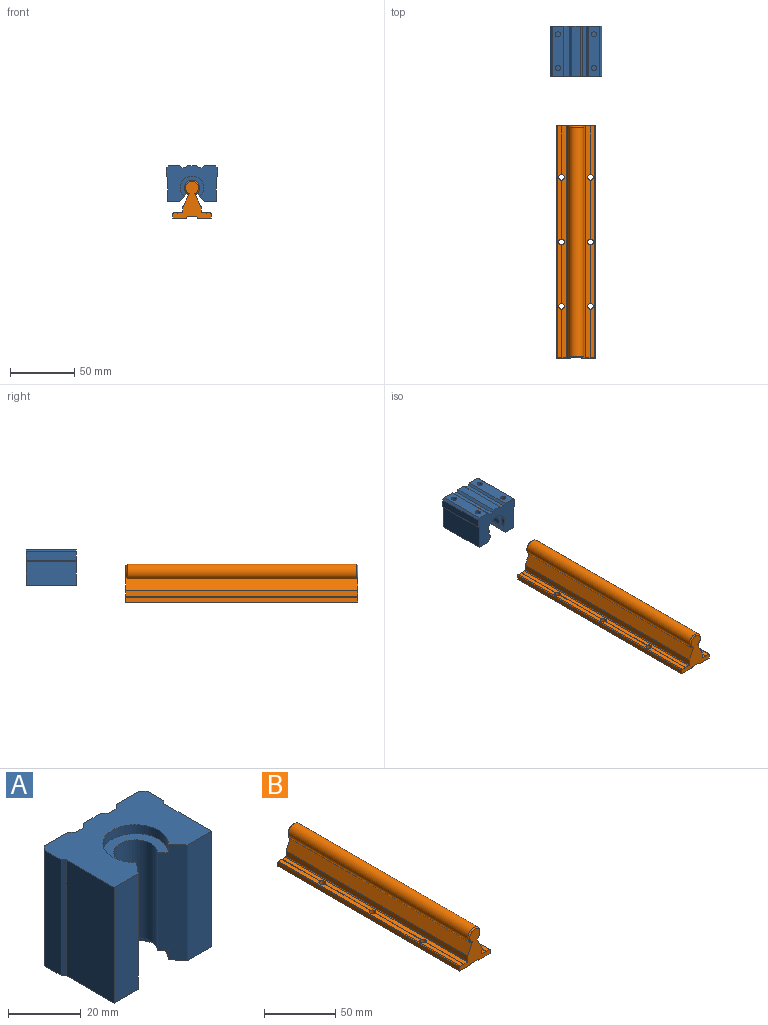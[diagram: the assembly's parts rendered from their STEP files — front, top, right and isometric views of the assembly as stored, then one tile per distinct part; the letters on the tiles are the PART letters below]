
ASSEMBLY  parts=2 mates=1
PART A: 36 faces, bbox 40x27.6x39 mm
  f0: cylinder r=6mm len=33mm, axis (0,0,-1), area 932.4mm2, adj f3,f4,f25,f35
  f1: plane 39x18.6mm, normal (-1,0,0), area 725.4mm2, adj f2,f21,f22,f23
  f2: plane 39x9.41mm, normal (0,-1,0), area 367mm2, adj f1,f3,f22,f23
  f3: plane 39x6.36mm, normal (0.77,-0.64,0), area 306mm2, adj f0,f2,f22,f23,f24,f25,f34,f35
  f4: plane 39x6.36mm, normal (-0.77,-0.64,0), area 306mm2, adj f0,f5,f22,f23,f24,f25,f34,f35
  f5: plane 39x9.41mm, normal (0,-1,0), area 367mm2, adj f4,f6,f22,f23
  f6: plane 39x18.6mm, normal (1,0,0), area 725.4mm2, adj f5,f7,f22,f23
  f7: plane 39x1mm, normal (0.71,-0.71,0), area 55.2mm2, adj f6,f8,f22,f23
  f8: plane 39x6.5mm, normal (1,0,0), area 253.5mm2, adj f7,f9,f22,f23
  f9: plane 39x1.5mm, normal (0.71,0.71,0), area 82.7mm2, adj f8,f10,f22,f23
  f10: plane 39x9mm, normal (0,1,0), area 325.9mm2, adj f9,f11,f22,f23,f30,f32
  f11: plane 39x1.62mm, normal (-0.68,0.73,0), area 86mm2, adj f10,f12,f22,f23
  f12: plane 39x3mm, normal (0,1,0), area 117mm2, adj f11,f13,f22,f23
  f13: plane 39x1.62mm, normal (0.68,0.73,0), area 86mm2, adj f12,f14,f22,f23
  f14: plane 39x6.53mm, normal (0,1,0), area 254.8mm2, adj f13,f15,f22,f23
  f15: plane 39x1.62mm, normal (-0.68,0.73,0), area 86mm2, adj f14,f16,f22,f23
  f16: plane 39x3mm, normal (0,1,0), area 117mm2, adj f15,f17,f22,f23
  f17: plane 39x1.62mm, normal (0.68,0.73,0), area 86mm2, adj f16,f18,f22,f23
  f18: plane 39x9mm, normal (0,1,0), area 325.9mm2, adj f17,f19,f22,f23,f26,f28
  f19: plane 39x1.5mm, normal (-0.71,0.71,0), area 82.7mm2, adj f18,f20,f22,f23
  f20: plane 39x6.5mm, normal (-1,0,0), area 253.5mm2, adj f19,f21,f22,f23
  f21: plane 39x1mm, normal (-0.71,-0.71,0), area 55.2mm2, adj f1,f20,f22,f23
  f22: plane 40x27.6mm, normal (0,0,1), area 752.1mm2, adj f1,f2,f3,f4,f5,f6,f7,f8
  f23: plane 40x27.6mm, normal (0,0,-1), area 752.1mm2, adj f1,f2,f3,f4,f5,f6,f7,f8
  f24: cylinder r=9mm len=18mm, axis (0,0,1), area 128.7mm2, adj f3,f4,f22,f25
  f25: plane 18x15.54mm, normal (0,0,1), area 106.8mm2, adj f0,f3,f4,f24
  f26: cylinder r=2mm len=10mm, axis (0,1,0), area 125.7mm2, adj f18,f27
  f27: plane 4x4mm, normal (0,1,0), area 12.6mm2, adj f26
  f28: cylinder r=2mm len=10mm, axis (0,1,0), area 125.7mm2, adj f18,f29
  f29: plane 4x4mm, normal (0,1,0), area 12.6mm2, adj f28
  f30: cylinder r=2mm len=10mm, axis (0,1,0), area 125.7mm2, adj f10,f31
  f31: plane 4x4mm, normal (0,1,0), area 12.6mm2, adj f30
  f32: cylinder r=2mm len=10mm, axis (0,1,0), area 125.7mm2, adj f10,f33
  f33: plane 4x4mm, normal (0,1,0), area 12.6mm2, adj f32
  f34: cylinder r=9mm len=18mm, axis (0,0,-1), area 128.7mm2, adj f3,f4,f23,f35
  f35: plane 18x15.54mm, normal (0,0,-1), area 106.8mm2, adj f0,f3,f4,f34
PART B: 58 faces, bbox 30x180x29.5 mm
  f0: plane 37.78x0.2mm, normal (1,0,0), area 7.6mm2, adj f32,f34,f49,f57
  f1: plane 37.76x0.2mm, normal (1,0,0), area 7.6mm2, adj f18,f46,f49,f56
  f2: plane 45.51x0.2mm, normal (-1,0,0), area 9.1mm2, adj f3,f30,f55,f57
  f3: plane 45.55x0.2mm, normal (0,0,1), area 9.1mm2, adj f2,f6,f55,f57
  f4: plane 45.55x0.2mm, normal (-1,0,0), area 9.1mm2, adj f5,f44,f54,f56
  f5: plane 45.55x0.2mm, normal (0,0,1), area 9.1mm2, adj f4,f7,f54,f56
  f6: plane 45.55x0.2mm, normal (1,0,0), area 9.1mm2, adj f3,f34,f55,f57
  f7: plane 45.51x0.2mm, normal (1,0,0), area 9.1mm2, adj f5,f18,f54,f56
  f8: plane 45.51x0.2mm, normal (-1,0,0), area 9.1mm2, adj f9,f30,f53,f55
  f9: plane 45.55x0.2mm, normal (0,0,1), area 9.1mm2, adj f8,f14,f53,f55
  f10: plane 45.55x0.2mm, normal (-1,0,0), area 9.1mm2, adj f11,f44,f52,f54
  f11: plane 45.55x0.2mm, normal (0,0,1), area 9.1mm2, adj f10,f17,f52,f54
  f12: plane 37.76x0.2mm, normal (-1,0,0), area 7.6mm2, adj f13,f30,f48,f53
  f13: plane 37.78x0.2mm, normal (0,0,1), area 7.6mm2, adj f12,f33,f48,f53
  f14: plane 45.55x0.2mm, normal (1,0,0), area 9.1mm2, adj f9,f34,f53,f55
  f15: plane 37.78x0.2mm, normal (-1,0,0), area 7.6mm2, adj f16,f44,f48,f52
  f16: plane 37.78x0.2mm, normal (0,0,1), area 7.6mm2, adj f15,f47,f48,f52
  f17: plane 45.51x0.2mm, normal (1,0,0), area 9.1mm2, adj f11,f18,f52,f54
  f18: plane 180x3.4mm, normal (0,0,1), area 586.1mm2, adj f1,f7,f17,f19,f47,f48,f49,f52
  f19: cylinder r=0.5mm len=180mm, axis (0,-1,0), area 141.4mm2, adj f18,f20,f48,f49
  f20: plane 180x3.5mm, normal (-1,0,0), area 630mm2, adj f19,f21,f48,f49
  f21: plane 180x11mm, normal (0,0,-1), area 1932.3mm2, adj f20,f22,f48,f49,f52,f54,f56
  f22: plane 180x0.5mm, normal (1,0,0), area 90mm2, adj f21,f23,f48,f49
  f23: cylinder r=0.5mm len=180mm, axis (0,-1,0), area 141.4mm2, adj f22,f24,f48,f49
  f24: plane 180x7mm, normal (0,0,-1), area 1260mm2, adj f23,f25,f48,f49
  f25: cylinder r=0.5mm len=180mm, axis (0,-1,0), area 141.4mm2, adj f24,f26,f48,f49
  f26: plane 180x0.5mm, normal (-1,0,0), area 90mm2, adj f25,f27,f48,f49
  f27: plane 180x11mm, normal (0,0,-1), area 1932.3mm2, adj f26,f28,f48,f49,f53,f55,f57
  f28: plane 180x3.5mm, normal (1,0,0), area 630mm2, adj f27,f29,f48,f49
  f29: cylinder r=0.5mm len=180mm, axis (0,-1,0), area 141.4mm2, adj f28,f30,f48,f49
  f30: plane 180x3.4mm, normal (0,0,1), area 586.1mm2, adj f2,f8,f12,f29,f31,f48,f49,f53
  f31: plane 37.76x0.2mm, normal (-1,0,0), area 7.6mm2, adj f30,f32,f49,f57
  f32: plane 37.78x0.2mm, normal (0,0,1), area 7.6mm2, adj f0,f31,f49,f57
  f33: plane 37.78x0.2mm, normal (1,0,0), area 7.6mm2, adj f13,f34,f48,f53
  f34: plane 180x3.4mm, normal (0,0,1), area 592.8mm2, adj f0,f6,f14,f33,f35,f48,f49,f53
  f35: cylinder r=0.5mm len=180mm, axis (0,-1,0), area 141.4mm2, adj f34,f36,f48,f49
  f36: plane 180x4.39mm, normal (1,0,0), area 789.4mm2, adj f35,f37,f48,f49
  f37: cylinder r=0.5mm len=180mm, axis (0,-1,0), area 40.5mm2, adj f36,f38,f48,f49
  f38: plane 180x9.89mm, normal (0.9,0,0.43), area 1798.6mm2, adj f37,f39,f48,f49,f50,f51
  f39: cylinder r=6mm len=178mm, axis (0,-1,0), area 5749.8mm2, adj f38,f40,f50,f51
  f40: plane 180x9.89mm, normal (-0.9,0,0.43), area 1798.6mm2, adj f39,f41,f48,f49,f50,f51
  f41: cylinder r=0.5mm len=180mm, axis (0,-1,0), area 40.5mm2, adj f40,f42,f48,f49
  f42: plane 180x4.39mm, normal (-1,0,0), area 789.4mm2, adj f41,f43,f48,f49
  f43: cylinder r=0.5mm len=180mm, axis (0,-1,0), area 141.4mm2, adj f42,f44,f48,f49
  f44: plane 180x3.4mm, normal (0,0,1), area 592.8mm2, adj f4,f10,f15,f43,f45,f48,f49,f52
  f45: plane 37.78x0.2mm, normal (-1,0,0), area 7.6mm2, adj f44,f46,f49,f56
  f46: plane 37.78x0.2mm, normal (0,0,1), area 7.6mm2, adj f1,f45,f49,f56
  f47: plane 37.76x0.2mm, normal (1,0,0), area 7.6mm2, adj f16,f18,f48,f52
  f48: plane 30x28.5mm, normal (0,1,0), area 350.8mm2, adj f12,f13,f15,f16,f18,f19,f20,f21
  f49: plane 30x28.5mm, normal (0,-1,0), area 350.8mm2, adj f0,f1,f18,f19,f20,f21,f22,f23
  f50: cone r=6mm half-angle=45deg, axis (0,1,0), area 41.9mm2, adj f38,f39,f40,f49
  f51: cone r=5mm half-angle=45deg, axis (0,-1,0), area 41.9mm2, adj f38,f39,f40,f48
  f52: cylinder r=2.25mm len=4.5mm, axis (0,0,-1), area 56.5mm2, adj f10,f11,f15,f16,f17,f18,f21,f44
  f53: cylinder r=2.25mm len=4.5mm, axis (0,0,-1), area 56.5mm2, adj f8,f9,f12,f13,f14,f27,f30,f33
  f54: cylinder r=2.25mm len=4.5mm, axis (0,0,-1), area 56.5mm2, adj f4,f5,f7,f10,f11,f17,f18,f21
  f55: cylinder r=2.25mm len=4.5mm, axis (0,0,-1), area 56.5mm2, adj f2,f3,f6,f8,f9,f14,f27,f30
  f56: cylinder r=2.25mm len=4.5mm, axis (0,0,-1), area 56.5mm2, adj f1,f4,f5,f7,f18,f21,f44,f45
  f57: cylinder r=2.25mm len=4.5mm, axis (0,0,-1), area 56.5mm2, adj f0,f2,f3,f6,f27,f30,f31,f32
PLACE A rot(axis=(1,0,0),90deg) t=(15.76,201.08,50.02)mm
PLACE B t=(0.76,-56.32,37.12)mm fixed
MATE slider A.f0 <-> B.f39  axis (0,1,0) through (15.76,181.58,60.62)mm
